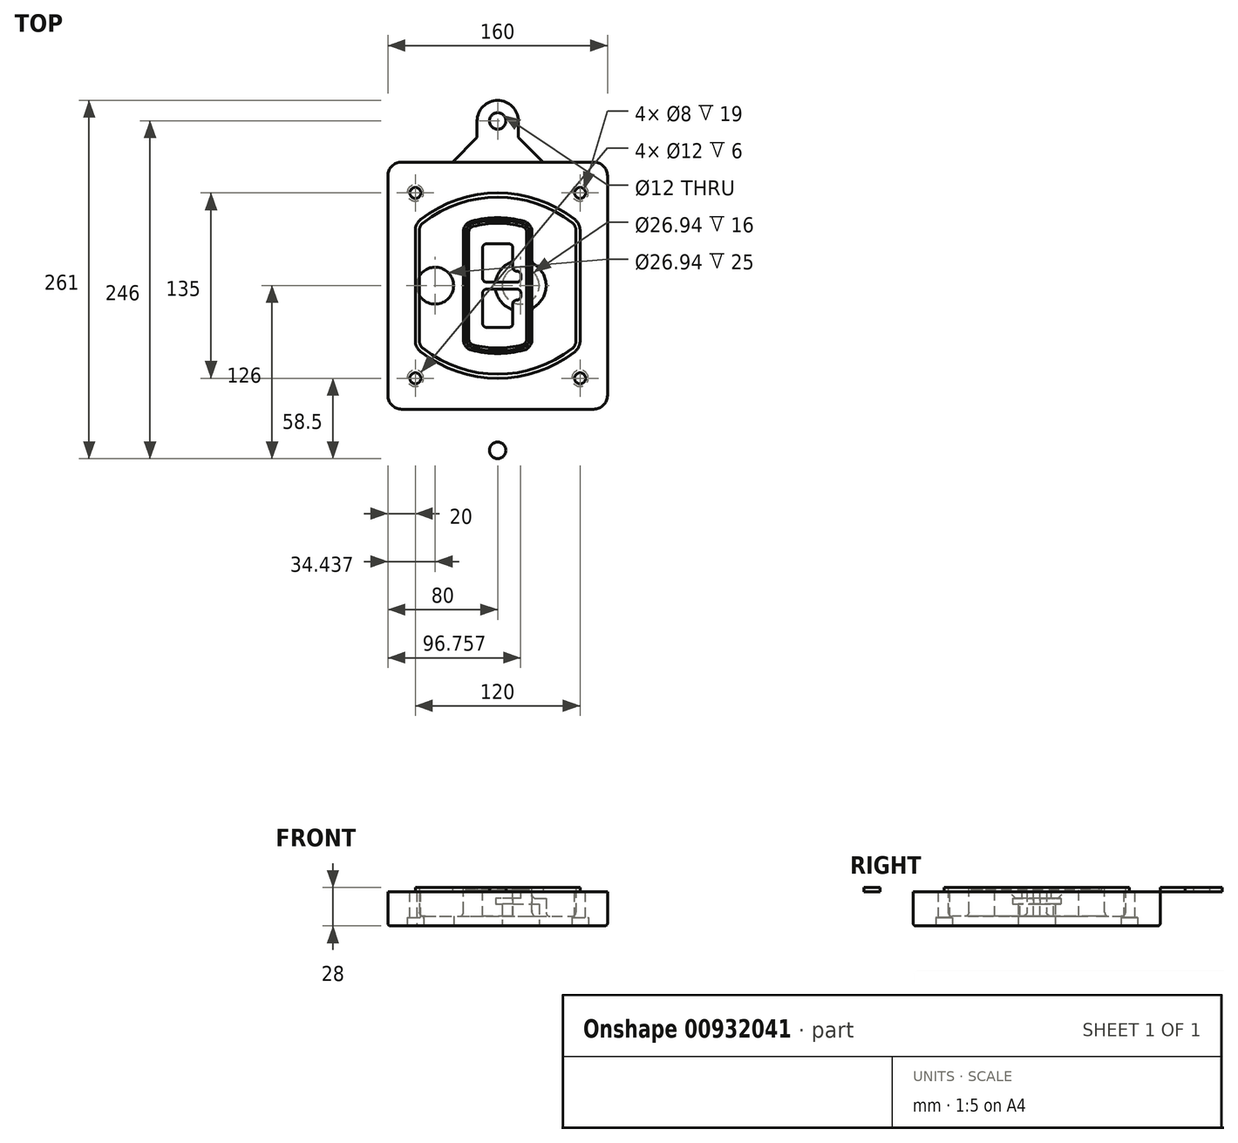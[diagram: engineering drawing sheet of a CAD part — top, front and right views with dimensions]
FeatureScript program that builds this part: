
annotation { "Feature Type Name" : "Feature", "Feature Type Description" : "" }
export const myFeature = defineFeature(function(context is Context, id is Id, definition is map)
    precondition{}
    {
        {
            var Q0;
            Q0=qCreatedBy(makeId("Top.planeOp"),FACE);
            var sketch = newSketch(context, id + "F0", { "sketchPlane" : qUnion([Q0])});
            skPoint(sketch, "E0.rect.middle", {"position": v(0, 0) * mm});
            skLineSegment(sketch, "E1.bottom", {"start": v(-70, -90) * mm, "end": v(70, -90) * mm});
            skLineSegment(sketch, "E1.top", {"start": v(-70, 90) * mm, "end": v(70, 90) * mm});
            skLineSegment(sketch, "E1.left", {"start": v(-80, -80) * mm, "end": v(-80, 80) * mm});
            skLineSegment(sketch, "E1.right", {"start": v(80, -80) * mm, "end": v(80, 80) * mm});
            skLineSegment(sketch, "E2", {"start": v(-80, 90) * mm, "end": v(80, -90) * mm, "construction": true});
            skLineSegment(sketch, "E3", {"start": v(80, 90) * mm, "end": v(-80, -90) * mm, "construction": true});
            skCircle(sketch, "E4", {"center": v(-60, 67.5) * mm, "radius": 4 * mm});
            skCircle(sketch, "E5", {"center": v(60, 67.5) * mm, "radius": 4 * mm});
            skCircle(sketch, "E6", {"center": v(60, -67.5) * mm, "radius": 4 * mm});
            skCircle(sketch, "E7", {"center": v(-60, -67.5) * mm, "radius": 4 * mm});
            skLineSegment(sketch, "E8", {"start": v(-60, 67.5) * mm, "end": v(60, 67.5) * mm, "construction": true});
            skLineSegment(sketch, "E9", {"start": v(60, 67.5) * mm, "end": v(60, -67.5) * mm, "construction": true});
            skLineSegment(sketch, "E10", {"start": v(60, -67.5) * mm, "end": v(-60, -67.5) * mm, "construction": true});
            skLineSegment(sketch, "E11", {"start": v(-60, -67.5) * mm, "end": v(-60, 67.5) * mm, "construction": true});
            skLineSegment(sketch, "E12", {"start": v(-60, 40.3) * mm, "end": v(-60, -40.3) * mm});
            skLineSegment(sketch, "E13", {"start": v(60, 40.3) * mm, "end": v(60, -40.3) * mm});
            skArc(sketch, "E14", {"start": v(56.15, 48.18) * mm, "mid": v(0, 67.5) * mm, "end": v(-56.15, 48.18) * mm});
            skArc(sketch, "E15", {"start": v(-56.15, -48.18) * mm, "mid": v(0, -67.5) * mm, "end": v(56.15, -48.18) * mm});
            skLineSegment(sketch, "E16", {"start": v(-60, 0) * mm, "end": v(60, 0) * mm, "construction": true});
            skPoint(sketch, "E17.visualSharp", {"position": v(-60, -45) * mm});
            skArc(sketch, "E17.filletArc", {"start": v(-60, -40.3) * mm, "mid": v(-58.99, -44.68) * mm, "end": v(-56.15, -48.18) * mm});
            skPoint(sketch, "E18.visualSharp", {"position": v(-60, 45) * mm});
            skArc(sketch, "E18.filletArc", {"start": v(-56.15, 48.18) * mm, "mid": v(-58.99, 44.68) * mm, "end": v(-60, 40.3) * mm});
            skPoint(sketch, "E19.visualSharp", {"position": v(60, 45) * mm});
            skArc(sketch, "E19.filletArc", {"start": v(60, 40.3) * mm, "mid": v(58.99, 44.68) * mm, "end": v(56.15, 48.18) * mm});
            skPoint(sketch, "E20.visualSharp", {"position": v(60, -45) * mm});
            skArc(sketch, "E20.filletArc", {"start": v(56.15, -48.18) * mm, "mid": v(58.99, -44.68) * mm, "end": v(60, -40.3) * mm});
            skPoint(sketch, "E21.visualSharp", {"position": v(-80, 90) * mm});
            skArc(sketch, "E21.filletArc", {"start": v(-70, 90) * mm, "mid": v(-77.07, 87.07) * mm, "end": v(-80, 80) * mm});
            skPoint(sketch, "E22.visualSharp", {"position": v(80, 90) * mm});
            skArc(sketch, "E22.filletArc", {"start": v(80, 80) * mm, "mid": v(77.07, 87.07) * mm, "end": v(70, 90) * mm});
            skPoint(sketch, "E23.visualSharp", {"position": v(80, -90) * mm});
            skArc(sketch, "E23.filletArc", {"start": v(70, -90) * mm, "mid": v(77.07, -87.07) * mm, "end": v(80, -80) * mm});
            skPoint(sketch, "E24.visualSharp", {"position": v(-80, -90) * mm});
            skArc(sketch, "E24.filletArc", {"start": v(-80, -80) * mm, "mid": v(-77.07, -87.07) * mm, "end": v(-70, -90) * mm});
            skArc(sketch, "E25.0", {"start": v(57, 40.3) * mm, "mid": v(56.3, 43.36) * mm, "end": v(54.3, 45.81) * mm});
            skLineSegment(sketch, "E25.1", {"start": v(57, 40.3) * mm, "end": v(57, -40.3) * mm});
            skArc(sketch, "E25.2", {"start": v(54.3, -45.81) * mm, "mid": v(56.3, -43.36) * mm, "end": v(57, -40.3) * mm});
            skArc(sketch, "E25.3", {"start": v(-54.3, -45.81) * mm, "mid": v(0, -64.5) * mm, "end": v(54.3, -45.81) * mm});
            skArc(sketch, "E25.4", {"start": v(-57, -40.3) * mm, "mid": v(-56.3, -43.36) * mm, "end": v(-54.3, -45.81) * mm});
            skArc(sketch, "E25.5", {"start": v(54.3, 45.81) * mm, "mid": v(0, 64.5) * mm, "end": v(-54.3, 45.81) * mm});
            skLineSegment(sketch, "E25.6", {"start": v(-57, 40.3) * mm, "end": v(-57, -40.3) * mm});
            skArc(sketch, "E25.7", {"start": v(-54.3, 45.81) * mm, "mid": v(-56.3, 43.36) * mm, "end": v(-57, 40.3) * mm});
            skArc(sketch, "E26.0", {"start": v(-58.62, 51.33) * mm, "mid": v(-62.58, 46.43) * mm, "end": v(-64, 40.3) * mm});
            skArc(sketch, "E26.1", {"start": v(58.62, 51.33) * mm, "mid": v(0, 71.5) * mm, "end": v(-58.62, 51.33) * mm});
            skArc(sketch, "E26.2", {"start": v(64, 40.3) * mm, "mid": v(62.58, 46.43) * mm, "end": v(58.62, 51.33) * mm});
            skLineSegment(sketch, "E26.3", {"start": v(64, 40.3) * mm, "end": v(64, -40.3) * mm});
            skArc(sketch, "E26.4", {"start": v(58.62, -51.33) * mm, "mid": v(62.58, -46.43) * mm, "end": v(64, -40.3) * mm});
            skLineSegment(sketch, "E26.5", {"start": v(-64, 40.3) * mm, "end": v(-64, -40.3) * mm});
            skArc(sketch, "E26.6", {"start": v(-58.62, -51.33) * mm, "mid": v(0, -71.5) * mm, "end": v(58.62, -51.33) * mm});
            skArc(sketch, "E26.7", {"start": v(-64, -40.3) * mm, "mid": v(-62.58, -46.43) * mm, "end": v(-58.62, -51.33) * mm});
            skSolve(sketch);
        }
        {
            var Q0;
            Q0=makeQuery(id+"F0.imprint","IMPRINT",FACE,{"disambiguationData":[TD([[makeQuery(id+"F0.imprint","IMPRINT",EDGE,{"derivedFrom":sQuery(id+"F0.wireOp",EDGE,"E1.bottom")}),1.0]])]});
            var Q1;
            Q1=makeQuery(id+"F0.imprint","IMPRINT",FACE,{"disambiguationData":[TD([[makeQuery(id+"F0.imprint","IMPRINT",EDGE,{"derivedFrom":sQuery(id+"F0.wireOp",EDGE,"E12")}),1.0]])]});
            var Q2;
            Q2=makeQuery(id+"F0.imprint","IMPRINT",FACE,{"disambiguationData":[TD([[makeQuery(id+"F0.imprint","IMPRINT",EDGE,{"derivedFrom":sQuery(id+"F0.wireOp",EDGE,"E25.0")}),1.0]])]});
            var Q3;
            Q3=makeQuery(id+"F0.imprint","IMPRINT",FACE,{"disambiguationData":[TD([[makeQuery(id+"F0.imprint","IMPRINT",EDGE,{"derivedFrom":sQuery(id+"F0.wireOp",EDGE,"E12")}),-1.0]])]});
            extrude(context, id + "F1", {"entities" : qUnion([Q0, Q1, Q2, Q3]), "oppositeDirection" : true, "depth" : 25 * mm});
        }
        {
            var Q0;
            Q0=makeQuery(id+"F0.imprint","IMPRINT",FACE,{"disambiguationData":[TD([[makeQuery(id+"F0.imprint","IMPRINT",EDGE,{"derivedFrom":sQuery(id+"F0.wireOp",EDGE,"E12")}),1.0]])]});
            extrude(context, id + "F2", {"entities" : qUnion([Q0]), "operationType" : NewBodyOperationType.ADD, "depth" : 3 * mm});
        }
        {
            var Q0;
            Q0=makeQuery(id+"F0.imprint","IMPRINT",FACE,{"disambiguationData":[TD([[makeQuery(id+"F0.imprint","IMPRINT",EDGE,{"derivedFrom":sQuery(id+"F0.wireOp",EDGE,"E25.0")}),1.0]])]});
            extrude(context, id + "F3", {"entities" : qUnion([Q0]), "operationType" : NewBodyOperationType.REMOVE, "oppositeDirection" : true, "depth" : 18 * mm});
        }
        {
            var Q0;
            Q0=makeQuery(id+"F2.opExtrude","CAP_FACE",FACE,{"disambiguationData":[OSD([sQuery(id+"F0.wireOp",EDGE,"E12"),sQuery(id+"F0.wireOp",EDGE,"E13"),sQuery(id+"F0.wireOp",EDGE,"E14"),sQuery(id+"F0.wireOp",EDGE,"E15"),sQuery(id+"F0.wireOp",EDGE,"E17.filletArc"),sQuery(id+"F0.wireOp",EDGE,"E18.filletArc"),sQuery(id+"F0.wireOp",EDGE,"E19.filletArc"),sQuery(id+"F0.wireOp",EDGE,"E20.filletArc"),sQuery(id+"F0.wireOp",EDGE,"E25.0"),sQuery(id+"F0.wireOp",EDGE,"E25.1"),sQuery(id+"F0.wireOp",EDGE,"E25.2"),sQuery(id+"F0.wireOp",EDGE,"E25.3"),sQuery(id+"F0.wireOp",EDGE,"E25.4"),sQuery(id+"F0.wireOp",EDGE,"E25.5"),sQuery(id+"F0.wireOp",EDGE,"E25.6"),sQuery(id+"F0.wireOp",EDGE,"E25.7")])],"isStart":false});
            var sketch = newSketch(context, id + "F4", { "sketchPlane" : qUnion([Q0])});
            skArc(sketch, "E27.0", {"start": v(-19.08, -46.97) * mm, "mid": v(0, -49.5) * mm, "end": v(19.08, -46.97) * mm});
            skArc(sketch, "E28.0", {"start": v(19.08, 46.97) * mm, "mid": v(0, 49.5) * mm, "end": v(-19.08, 46.97) * mm});
            skLineSegment(sketch, "E29", {"start": v(-25, 39.25) * mm, "end": v(-25, -39.25) * mm});
            skLineSegment(sketch, "E30", {"start": v(25, 39.25) * mm, "end": v(25, -39.25) * mm});
            skLineSegment(sketch, "E31", {"start": v(-25, 45.1) * mm, "end": v(25, 45.1) * mm, "construction": true});
            skLineSegment(sketch, "E32", {"start": v(-25, -45.1) * mm, "end": v(25, -45.1) * mm, "construction": true});
            skPoint(sketch, "E33.visualSharp", {"position": v(-25, 45.1) * mm});
            skArc(sketch, "E33.filletArc", {"start": v(-19.08, 46.97) * mm, "mid": v(-23.35, 44.11) * mm, "end": v(-25, 39.25) * mm});
            skPoint(sketch, "E34.visualSharp", {"position": v(25, 45.1) * mm});
            skArc(sketch, "E34.filletArc", {"start": v(25, 39.25) * mm, "mid": v(23.35, 44.11) * mm, "end": v(19.08, 46.97) * mm});
            skPoint(sketch, "E35.visualSharp", {"position": v(25, -45.1) * mm});
            skArc(sketch, "E35.filletArc", {"start": v(19.08, -46.97) * mm, "mid": v(23.35, -44.11) * mm, "end": v(25, -39.25) * mm});
            skPoint(sketch, "E36.visualSharp", {"position": v(-25, -45.1) * mm});
            skArc(sketch, "E36.filletArc", {"start": v(-25, -39.25) * mm, "mid": v(-23.35, -44.11) * mm, "end": v(-19.08, -46.97) * mm});
            skArc(sketch, "E37.0", {"start": v(54.3, 45.81) * mm, "mid": v(0, 64.5) * mm, "end": v(-54.3, 45.81) * mm});
            skArc(sketch, "E37.1", {"start": v(-54.3, 45.81) * mm, "mid": v(-56.3, 43.36) * mm, "end": v(-57, 40.3) * mm});
            skLineSegment(sketch, "E37.2", {"start": v(-57, 40.3) * mm, "end": v(-57, -40.3) * mm});
            skArc(sketch, "E37.3", {"start": v(-57, -40.3) * mm, "mid": v(-56.3, -43.36) * mm, "end": v(-54.3, -45.81) * mm});
            skArc(sketch, "E37.4", {"start": v(-54.3, -45.81) * mm, "mid": v(0, -64.5) * mm, "end": v(54.3, -45.81) * mm});
            skArc(sketch, "E37.5", {"start": v(54.3, -45.81) * mm, "mid": v(56.3, -43.36) * mm, "end": v(57, -40.3) * mm});
            skLineSegment(sketch, "E37.6", {"start": v(57, 40.3) * mm, "end": v(57, -40.3) * mm});
            skArc(sketch, "E37.7", {"start": v(57, 40.3) * mm, "mid": v(56.3, 43.36) * mm, "end": v(54.3, 45.81) * mm});
            skLineSegment(sketch, "E38.0", {"start": v(23, 39.25) * mm, "end": v(23, -39.25) * mm});
            skArc(sketch, "E38.1", {"start": v(18.56, -45.04) * mm, "mid": v(21.76, -42.9) * mm, "end": v(23, -39.25) * mm});
            skArc(sketch, "E38.2", {"start": v(-18.56, -45.04) * mm, "mid": v(0, -47.5) * mm, "end": v(18.56, -45.04) * mm});
            skArc(sketch, "E38.3", {"start": v(-23, -39.25) * mm, "mid": v(-21.76, -42.9) * mm, "end": v(-18.56, -45.04) * mm});
            skLineSegment(sketch, "E38.4", {"start": v(-23, 39.25) * mm, "end": v(-23, -39.25) * mm});
            skArc(sketch, "E38.5", {"start": v(23, 39.25) * mm, "mid": v(21.76, 42.9) * mm, "end": v(18.56, 45.04) * mm});
            skArc(sketch, "E38.6", {"start": v(-18.56, 45.04) * mm, "mid": v(-21.76, 42.9) * mm, "end": v(-23, 39.25) * mm});
            skArc(sketch, "E38.7", {"start": v(18.56, 45.04) * mm, "mid": v(0, 47.5) * mm, "end": v(-18.56, 45.04) * mm});
            skArc(sketch, "E39.0", {"start": v(21, 39.25) * mm, "mid": v(20.18, 41.68) * mm, "end": v(18.04, 43.1) * mm});
            skLineSegment(sketch, "E39.1", {"start": v(21, 39.25) * mm, "end": v(21, -39.25) * mm});
            skArc(sketch, "E39.2", {"start": v(18.04, -43.1) * mm, "mid": v(20.18, -41.68) * mm, "end": v(21, -39.25) * mm});
            skArc(sketch, "E39.3", {"start": v(-18.04, -43.1) * mm, "mid": v(0, -45.5) * mm, "end": v(18.04, -43.1) * mm});
            skArc(sketch, "E39.4", {"start": v(-21, -39.25) * mm, "mid": v(-20.18, -41.68) * mm, "end": v(-18.04, -43.1) * mm});
            skArc(sketch, "E39.5", {"start": v(18.04, 43.1) * mm, "mid": v(0, 45.5) * mm, "end": v(-18.04, 43.1) * mm});
            skLineSegment(sketch, "E39.6", {"start": v(-21, 39.25) * mm, "end": v(-21, -39.25) * mm});
            skArc(sketch, "E39.7", {"start": v(-18.04, 43.1) * mm, "mid": v(-20.18, 41.68) * mm, "end": v(-21, 39.25) * mm});
            skLineSegment(sketch, "E40", {"start": v(-25, 0) * mm, "end": v(25, 0) * mm, "construction": true});
            skLineSegment(sketch, "E41", {"start": v(-11, 5.5) * mm, "end": v(-11, 27.5) * mm});
            skLineSegment(sketch, "E42", {"start": v(-8, 30.5) * mm, "end": v(8, 30.5) * mm});
            skLineSegment(sketch, "E43", {"start": v(11, 27.5) * mm, "end": v(11, 13.5) * mm});
            skLineSegment(sketch, "E44", {"start": v(14, 10.5) * mm, "end": v(14, 10.5) * mm});
            skLineSegment(sketch, "E45", {"start": v(17, 7.5) * mm, "end": v(17, 5.5) * mm});
            skLineSegment(sketch, "E46", {"start": v(14, 2.5) * mm, "end": v(-8, 2.5) * mm});
            skPoint(sketch, "E47.visualSharp", {"position": v(-11, 30.5) * mm});
            skArc(sketch, "E47.filletArc", {"start": v(-8, 30.5) * mm, "mid": v(-10.12, 29.62) * mm, "end": v(-11, 27.5) * mm});
            skPoint(sketch, "E48.visualSharp", {"position": v(11, 30.5) * mm});
            skArc(sketch, "E48.filletArc", {"start": v(11, 27.5) * mm, "mid": v(10.12, 29.62) * mm, "end": v(8, 30.5) * mm});
            skPoint(sketch, "E49.visualSharp", {"position": v(11, 10.5) * mm});
            skArc(sketch, "E49.filletArc", {"start": v(11, 13.5) * mm, "mid": v(11.88, 11.38) * mm, "end": v(14, 10.5) * mm});
            skPoint(sketch, "E50.visualSharp", {"position": v(17, 10.5) * mm});
            skArc(sketch, "E50.filletArc", {"start": v(17, 7.5) * mm, "mid": v(16.12, 9.62) * mm, "end": v(14, 10.5) * mm});
            skPoint(sketch, "E51.visualSharp", {"position": v(17, 2.5) * mm});
            skArc(sketch, "E51.filletArc", {"start": v(14, 2.5) * mm, "mid": v(16.12, 3.38) * mm, "end": v(17, 5.5) * mm});
            skPoint(sketch, "E52.visualSharp", {"position": v(-11, 2.5) * mm});
            skArc(sketch, "E52.filletArc", {"start": v(-11, 5.5) * mm, "mid": v(-10.12, 3.38) * mm, "end": v(-8, 2.5) * mm});
            skLineSegment(sketch, "E53.0.MirrorCS", {"start": v(14, -2.5) * mm, "end": v(-8, -2.5) * mm});
            skArc(sketch, "E54.0.MirrorCS", {"start": v(-11, -5.5) * mm, "mid": v(-10.12, -3.38) * mm, "end": v(-8, -2.5) * mm});
            skLineSegment(sketch, "E55.0.MirrorCS", {"start": v(-11, -5.5) * mm, "end": v(-11, -27.5) * mm});
            skArc(sketch, "E56.0.MirrorCS", {"start": v(-8, -30.5) * mm, "mid": v(-10.12, -29.62) * mm, "end": v(-11, -27.5) * mm});
            skLineSegment(sketch, "E57.0.MirrorCS", {"start": v(-8, -30.5) * mm, "end": v(8, -30.5) * mm});
            skArc(sketch, "E58.0.MirrorCS", {"start": v(11, -27.5) * mm, "mid": v(10.12, -29.62) * mm, "end": v(8, -30.5) * mm});
            skLineSegment(sketch, "E59.0.MirrorCS", {"start": v(11, -27.5) * mm, "end": v(11, -13.5) * mm});
            skArc(sketch, "E60.0.MirrorCS", {"start": v(11, -13.5) * mm, "mid": v(11.88, -11.38) * mm, "end": v(14, -10.5) * mm});
            skArc(sketch, "E61.0.MirrorCS", {"start": v(17, -7.5) * mm, "mid": v(16.12, -9.62) * mm, "end": v(14, -10.5) * mm});
            skLineSegment(sketch, "E62.0.MirrorCS", {"start": v(17, -7.5) * mm, "end": v(17, -5.5) * mm});
            skArc(sketch, "E63.0.MirrorCS", {"start": v(14, -2.5) * mm, "mid": v(16.12, -3.38) * mm, "end": v(17, -5.5) * mm});
            skSolve(sketch);
        }
        {
            var Q0;
            Q0=makeQuery(id+"F4.imprint","IMPRINT",FACE,{"disambiguationData":[TD([[makeQuery(id+"F4.imprint","IMPRINT",EDGE,{"derivedFrom":sQuery(id+"F4.wireOp",EDGE,"E27.0")}),1.0]])]});
            var Q1;
            Q1=makeQuery(id+"F4.imprint","IMPRINT",FACE,{"disambiguationData":[TD([[makeQuery(id+"F4.imprint","IMPRINT",EDGE,{"derivedFrom":sQuery(id+"F4.wireOp",EDGE,"E38.0")}),-1.0]])]});
            var Q2;
            Q2=makeQuery(id+"F4.imprint","IMPRINT",FACE,{"disambiguationData":[TD([[makeQuery(id+"F4.imprint","IMPRINT",EDGE,{"derivedFrom":sQuery(id+"F4.wireOp",EDGE,"E39.0")}),1.0]])]});
            extrude(context, id + "F5", {"entities" : qUnion([Q0, Q1, Q2]), "operationType" : NewBodyOperationType.ADD, "endBound" : BoundingType.UP_TO_NEXT, "oppositeDirection" : true, "depth" : 25 * mm});
        }
        {
            var Q0;
            Q0=makeQuery(id+"F4.imprint","IMPRINT",FACE,{"disambiguationData":[TD([[makeQuery(id+"F4.imprint","IMPRINT",EDGE,{"derivedFrom":sQuery(id+"F4.wireOp",EDGE,"E38.0")}),-1.0]])]});
            extrude(context, id + "F6", {"entities" : qUnion([Q0]), "operationType" : NewBodyOperationType.REMOVE, "oppositeDirection" : true, "depth" : 2 * mm});
        }
        {
            var Q0;
            Q0=makeQuery(id+"F1.opExtrude","CAP_FACE",FACE,{"disambiguationData":[OSD([sQuery(id+"F0.wireOp",EDGE,"E1.bottom"),sQuery(id+"F0.wireOp",EDGE,"E1.top"),sQuery(id+"F0.wireOp",EDGE,"E1.left"),sQuery(id+"F0.wireOp",EDGE,"E1.right"),sQuery(id+"F0.wireOp",EDGE,"E4"),sQuery(id+"F0.wireOp",EDGE,"E5"),sQuery(id+"F0.wireOp",EDGE,"E6"),sQuery(id+"F0.wireOp",EDGE,"E7"),sQuery(id+"F0.wireOp",EDGE,"E21.filletArc"),sQuery(id+"F0.wireOp",EDGE,"E22.filletArc"),sQuery(id+"F0.wireOp",EDGE,"E23.filletArc"),sQuery(id+"F0.wireOp",EDGE,"E24.filletArc")])],"isStart":false});
            var sketch = newSketch(context, id + "F7", { "sketchPlane" : qUnion([Q0])});
            skCircle(sketch, "E64", {"center": v(16.76, 0) * mm, "radius": 13.47 * mm});
            skCircle(sketch, "E65", {"center": v(-45.56, 0) * mm, "radius": 13.47 * mm});
            skLineSegment(sketch, "E66", {"start": v(80, 0) * mm, "end": v(-80, 0) * mm});
            skCircle(sketch, "E67", {"center": v(16.76, 0) * mm, "radius": 18.47 * mm});
            skCircle(sketch, "E68", {"center": v(60, -67.5) * mm, "radius": 6 * mm});
            skCircle(sketch, "E69", {"center": v(-60, -67.5) * mm, "radius": 6 * mm});
            skCircle(sketch, "E70", {"center": v(-60, 67.5) * mm, "radius": 6 * mm});
            skCircle(sketch, "E71", {"center": v(60, 67.5) * mm, "radius": 6 * mm});
            skSolve(sketch);
        }
        {
            var Q0;
            {var subQ1=sQuery(id+"F7.wireOp",EDGE,"E66");var subQ4=sQuery(id+"F7.wireOp",EDGE,"E64");var subQ6=makeQuery(id+"F7.imprint","INTERSECT",VERTEX,{"disambiguationData":[OD(0.0)],"derivedFrom":[subQ4,subQ1]});Q0=makeQuery(id+"F7.imprint","IMPRINT",FACE,{"disambiguationData":[TD([[makeQuery(id+"F7.imprint","IMPRINT",EDGE,{"disambiguationData":[TD([[subQ6,-1.0]])],"derivedFrom":subQ4}),-1.0]])]});}
            var Q1;
            {var subQ0=sQuery(id+"F7.wireOp",EDGE,"E66");var subQ1=sQuery(id+"F7.wireOp",EDGE,"E64");var subQ3=makeQuery(id+"F7.imprint","INTERSECT",VERTEX,{"disambiguationData":[OD(0.0)],"derivedFrom":[subQ1,subQ0]});Q1=makeQuery(id+"F7.imprint","IMPRINT",FACE,{"disambiguationData":[TD([[makeQuery(id+"F7.imprint","IMPRINT",EDGE,{"disambiguationData":[TD([[subQ3,-1.0]])],"derivedFrom":subQ1}),1.0]])]});}
            var Q2;
            {var subQ0=sQuery(id+"F7.wireOp",EDGE,"E66");var subQ1=sQuery(id+"F7.wireOp",EDGE,"E64");var subQ3=makeQuery(id+"F7.imprint","INTERSECT",VERTEX,{"disambiguationData":[OD(0.0)],"derivedFrom":[subQ1,subQ0]});Q2=makeQuery(id+"F7.imprint","IMPRINT",FACE,{"disambiguationData":[TD([[makeQuery(id+"F7.imprint","IMPRINT",EDGE,{"disambiguationData":[TD([[subQ3,1.0]])],"derivedFrom":subQ1}),1.0]])]});}
            var Q3;
            {var subQ1=sQuery(id+"F7.wireOp",EDGE,"E66");var subQ4=sQuery(id+"F7.wireOp",EDGE,"E64");var subQ6=makeQuery(id+"F7.imprint","INTERSECT",VERTEX,{"disambiguationData":[OD(0.0)],"derivedFrom":[subQ4,subQ1]});Q3=makeQuery(id+"F7.imprint","IMPRINT",FACE,{"disambiguationData":[TD([[makeQuery(id+"F7.imprint","IMPRINT",EDGE,{"disambiguationData":[TD([[subQ6,1.0]])],"derivedFrom":subQ4}),-1.0]])]});}
            extrude(context, id + "F8", {"entities" : qUnion([Q0, Q1, Q2, Q3]), "operationType" : NewBodyOperationType.ADD, "oppositeDirection" : true, "depth" : 20 * mm});
        }
        {
            var Q0;
            {var subQ0=sQuery(id+"F7.wireOp",EDGE,"E66");var subQ1=sQuery(id+"F7.wireOp",EDGE,"E64");var subQ3=makeQuery(id+"F7.imprint","INTERSECT",VERTEX,{"disambiguationData":[OD(0.0)],"derivedFrom":[subQ1,subQ0]});Q0=makeQuery(id+"F7.imprint","IMPRINT",FACE,{"disambiguationData":[TD([[makeQuery(id+"F7.imprint","IMPRINT",EDGE,{"disambiguationData":[TD([[subQ3,-1.0]])],"derivedFrom":subQ1}),1.0]])]});}
            var Q1;
            {var subQ0=sQuery(id+"F7.wireOp",EDGE,"E66");var subQ1=sQuery(id+"F7.wireOp",EDGE,"E64");var subQ3=makeQuery(id+"F7.imprint","INTERSECT",VERTEX,{"disambiguationData":[OD(0.0)],"derivedFrom":[subQ1,subQ0]});Q1=makeQuery(id+"F7.imprint","IMPRINT",FACE,{"disambiguationData":[TD([[makeQuery(id+"F7.imprint","IMPRINT",EDGE,{"disambiguationData":[TD([[subQ3,1.0]])],"derivedFrom":subQ1}),1.0]])]});}
            extrude(context, id + "F9", {"entities" : qUnion([Q0, Q1]), "operationType" : NewBodyOperationType.REMOVE, "oppositeDirection" : true, "depth" : 16 * mm});
        }
        {
            var Q0;
            {var subQ0=sQuery(id+"F7.wireOp",EDGE,"E66");var subQ1=sQuery(id+"F7.wireOp",EDGE,"E65");var subQ3=makeQuery(id+"F7.imprint","INTERSECT",VERTEX,{"disambiguationData":[OD(0.0)],"derivedFrom":[subQ1,subQ0]});Q0=makeQuery(id+"F7.imprint","IMPRINT",FACE,{"disambiguationData":[TD([[makeQuery(id+"F7.imprint","IMPRINT",EDGE,{"disambiguationData":[TD([[subQ3,-1.0]])],"derivedFrom":subQ1}),1.0]])]});}
            var Q1;
            {var subQ0=sQuery(id+"F7.wireOp",EDGE,"E66");var subQ1=sQuery(id+"F7.wireOp",EDGE,"E65");var subQ3=makeQuery(id+"F7.imprint","INTERSECT",VERTEX,{"disambiguationData":[OD(0.0)],"derivedFrom":[subQ1,subQ0]});Q1=makeQuery(id+"F7.imprint","IMPRINT",FACE,{"disambiguationData":[TD([[makeQuery(id+"F7.imprint","IMPRINT",EDGE,{"disambiguationData":[TD([[subQ3,1.0]])],"derivedFrom":subQ1}),1.0]])]});}
            extrude(context, id + "F10", {"entities" : qUnion([Q0, Q1]), "operationType" : NewBodyOperationType.REMOVE, "oppositeDirection" : true, "depth" : 25 * mm});
        }
        {
            var Q0;
            Q0=makeQuery(id+"F7.imprint","IMPRINT",FACE,{"disambiguationData":[TD([[makeQuery(id+"F7.imprint","IMPRINT",EDGE,{"derivedFrom":sQuery(id+"F7.wireOp",EDGE,"E68")}),1.0]])]});
            var Q1;
            Q1=makeQuery(id+"F7.imprint","IMPRINT",FACE,{"disambiguationData":[TD([[makeQuery(id+"F7.imprint","IMPRINT",EDGE,{"derivedFrom":makeQuery(id+"F1.opExtrude","CAP_EDGE",EDGE,{"disambiguationData":[OSD([sQuery(id+"F0.wireOp",EDGE,"E5")])],"isStart":false})}),-1.0]])]});
            var Q2;
            Q2=makeQuery(id+"F7.imprint","IMPRINT",FACE,{"disambiguationData":[TD([[makeQuery(id+"F7.imprint","IMPRINT",EDGE,{"derivedFrom":sQuery(id+"F7.wireOp",EDGE,"E69")}),1.0]])]});
            var Q3;
            Q3=makeQuery(id+"F7.imprint","IMPRINT",FACE,{"disambiguationData":[TD([[makeQuery(id+"F7.imprint","IMPRINT",EDGE,{"derivedFrom":makeQuery(id+"F1.opExtrude","CAP_EDGE",EDGE,{"disambiguationData":[OSD([sQuery(id+"F0.wireOp",EDGE,"E4")])],"isStart":false})}),-1.0]])]});
            var Q4;
            Q4=makeQuery(id+"F7.imprint","IMPRINT",FACE,{"disambiguationData":[TD([[makeQuery(id+"F7.imprint","IMPRINT",EDGE,{"derivedFrom":sQuery(id+"F7.wireOp",EDGE,"E70")}),1.0]])]});
            var Q5;
            Q5=makeQuery(id+"F7.imprint","IMPRINT",FACE,{"disambiguationData":[TD([[makeQuery(id+"F7.imprint","IMPRINT",EDGE,{"derivedFrom":makeQuery(id+"F1.opExtrude","CAP_EDGE",EDGE,{"disambiguationData":[OSD([sQuery(id+"F0.wireOp",EDGE,"E7")])],"isStart":false})}),-1.0]])]});
            var Q6;
            Q6=makeQuery(id+"F7.imprint","IMPRINT",FACE,{"disambiguationData":[TD([[makeQuery(id+"F7.imprint","IMPRINT",EDGE,{"derivedFrom":sQuery(id+"F7.wireOp",EDGE,"E71")}),1.0]])]});
            var Q7;
            Q7=makeQuery(id+"F7.imprint","IMPRINT",FACE,{"disambiguationData":[TD([[makeQuery(id+"F7.imprint","IMPRINT",EDGE,{"derivedFrom":makeQuery(id+"F1.opExtrude","CAP_EDGE",EDGE,{"disambiguationData":[OSD([sQuery(id+"F0.wireOp",EDGE,"E6")])],"isStart":false})}),-1.0]])]});
            extrude(context, id + "F11", {"entities" : qUnion([Q0, Q1, Q2, Q3, Q4, Q5, Q6, Q7]), "operationType" : NewBodyOperationType.REMOVE, "oppositeDirection" : true, "depth" : 6 * mm});
        }
        {
            var Q0;
            Q0=makeQuery(id+"F9.boolean.opBoolean","COPY",FACE,{"derivedFrom":makeQuery(id+"F9.opExtrude","CAP_FACE",FACE,{"disambiguationData":[OSD([sQuery(id+"F7.wireOp",EDGE,"E64")])],"isStart":false})});
            var sketch = newSketch(context, id + "F12", { "sketchPlane" : qUnion([Q0])});
            skArc(sketch, "E72.0", {"start": v(11, 17.55) * mm, "mid": v(2.57, 11.82) * mm, "end": v(-1.54, 2.5) * mm});
            skArc(sketch, "E72.1", {"start": v(-1.54, -2.5) * mm, "mid": v(2.57, -11.82) * mm, "end": v(11, -17.55) * mm});
            skLineSegment(sketch, "E73", {"start": v(-1.54, -2.5) * mm, "end": v(14, -2.5) * mm});
            skLineSegment(sketch, "E74.0", {"start": v(14, 2.5) * mm, "end": v(-1.54, 2.5) * mm});
            skArc(sketch, "E74.1", {"start": v(14, 2.5) * mm, "mid": v(16.12, 3.38) * mm, "end": v(17, 5.5) * mm});
            skLineSegment(sketch, "E74.2", {"start": v(17, 7.5) * mm, "end": v(17, 5.5) * mm});
            skArc(sketch, "E74.3", {"start": v(17, 7.5) * mm, "mid": v(16.12, 9.62) * mm, "end": v(14, 10.5) * mm});
            skArc(sketch, "E74.4", {"start": v(11, 13.5) * mm, "mid": v(11.88, 11.38) * mm, "end": v(14, 10.5) * mm});
            skLineSegment(sketch, "E74.5", {"start": v(11, 17.55) * mm, "end": v(11, 13.5) * mm});
            skLineSegment(sketch, "E74.7", {"start": v(14, -2.5) * mm, "end": v(-1.54, -2.5) * mm});
            skArc(sketch, "E74.8", {"start": v(14, -2.5) * mm, "mid": v(16.12, -3.38) * mm, "end": v(17, -5.5) * mm});
            skLineSegment(sketch, "E74.9", {"start": v(17, -7.5) * mm, "end": v(17, -5.5) * mm});
            skArc(sketch, "E74.10", {"start": v(17, -7.5) * mm, "mid": v(16.12, -9.62) * mm, "end": v(14, -10.5) * mm});
            skArc(sketch, "E74.11", {"start": v(11, -13.5) * mm, "mid": v(11.88, -11.38) * mm, "end": v(14, -10.5) * mm});
            skLineSegment(sketch, "E74.12", {"start": v(11, -17.55) * mm, "end": v(11, -13.5) * mm});
            skPoint(sketch, "E75.orphan", {"position": v(11, -27.5) * mm});
            skPoint(sketch, "E76.orphan", {"position": v(-8, -2.5) * mm});
            skPoint(sketch, "E77.orphan", {"position": v(-8, 2.5) * mm});
            skPoint(sketch, "E78.orphan", {"position": v(11, 27.5) * mm});
            skSolve(sketch);
        }
        {
            var Q0;
            {var subQ7=sQuery(id+"F12.wireOp",EDGE,"E72.0");var subQ14=sQuery(id+"F12.wireOp",EDGE,"E72.1");var subQ16=sQuery(id+"F12.wireOp",EDGE,"E74.1");var subQ18=sQuery(id+"F12.wireOp",EDGE,"E74.8");Q0=qUnion([makeQuery(id+"F12.imprint","IMPRINT",FACE,{"disambiguationData":[TD([[makeQuery(id+"F12.imprint","IMPRINT",EDGE,{"derivedFrom":subQ7}),1.0]])]}),makeQuery(id+"F12.imprint","IMPRINT",FACE,{"disambiguationData":[TD([[makeQuery(id+"F12.imprint","IMPRINT",EDGE,{"derivedFrom":subQ14}),1.0]])]}),makeQuery(id+"F12.imprint","IMPRINT",FACE,{"disambiguationData":[TD([[makeQuery(id+"F12.imprint","IMPRINT",EDGE,{"derivedFrom":subQ16}),1.0]])]}),makeQuery(id+"F12.imprint","IMPRINT",FACE,{"disambiguationData":[TD([[makeQuery(id+"F12.imprint","IMPRINT",EDGE,{"derivedFrom":subQ18}),-1.0]])]})]);}
            var Q1;
            Q1=makeQuery(id+"F5.boolean.opBoolean","SPLIT",FACE,{"disambiguationData":[TD([makeQuery(id+"F5.opExtrude","SWEPT_FACE",FACE,{"disambiguationData":[OSD([sQuery(id+"F4.wireOp",EDGE,"E41")])]})])],"derivedFrom":makeQuery(id+"F3.boolean.opBoolean","COPY",FACE,{"derivedFrom":makeQuery(id+"F3.opExtrude","CAP_FACE",FACE,{"disambiguationData":[OSD([sQuery(id+"F0.wireOp",EDGE,"E25.0"),sQuery(id+"F0.wireOp",EDGE,"E25.1"),sQuery(id+"F0.wireOp",EDGE,"E25.2"),sQuery(id+"F0.wireOp",EDGE,"E25.3"),sQuery(id+"F0.wireOp",EDGE,"E25.4"),sQuery(id+"F0.wireOp",EDGE,"E25.5"),sQuery(id+"F0.wireOp",EDGE,"E25.6"),sQuery(id+"F0.wireOp",EDGE,"E25.7")])],"isStart":false})})});
            extrude(context, id + "F13", {"entities" : qUnion([Q0]), "operationType" : NewBodyOperationType.REMOVE, "endBound" : BoundingType.UP_TO_SURFACE, "endBoundEntityFace" : qUnion([Q1]), "depth" : 25 * mm});
        }
        {
            var Q0;
            Q0=makeQuery(id+"F3.boolean.opBoolean","COPY",EDGE,{"derivedFrom":makeQuery(id+"F3.opExtrude","CAP_EDGE",EDGE,{"disambiguationData":[OSD([sQuery(id+"F0.wireOp",EDGE,"E25.6")])],"isStart":false})});
            var Q1;
            Q1=makeQuery(id+"F8.boolean.opBoolean","INTERSECT",EDGE,{"derivedFrom":[makeQuery(id+"F5.opExtrude","SWEPT_FACE",FACE,{"disambiguationData":[OSD([sQuery(id+"F4.wireOp",EDGE,"E30")])]}),makeQuery(id+"F8.opExtrude","CAP_FACE",FACE,{"disambiguationData":[OSD([sQuery(id+"F7.wireOp",EDGE,"E67")])],"isStart":false})]});
            var Q2;
            Q2=makeQuery(id+"F8.boolean.opBoolean","INTERSECT",EDGE,{"disambiguationData":[OD(1.0)],"derivedFrom":[makeQuery(id+"F5.opExtrude","SWEPT_FACE",FACE,{"disambiguationData":[OSD([sQuery(id+"F4.wireOp",EDGE,"E30")])]}),makeQuery(id+"F8.opExtrude","SWEPT_FACE",FACE,{"disambiguationData":[OSD([sQuery(id+"F7.wireOp",EDGE,"E67")])]})]});
            var Q3;
            {var subQ0=sQuery(id+"F4.wireOp",EDGE,"E30");Q3=makeQuery(id+"F8.boolean.opBoolean","SPLIT",EDGE,{"disambiguationData":[TD([makeQuery(id+"F5.opExtrude","SWEPT_FACE",FACE,{"disambiguationData":[OSD([sQuery(id+"F4.wireOp",EDGE,"E35.filletArc")])]})])],"derivedFrom":makeQuery(id+"F5.opExtrude","CAP_EDGE",EDGE,{"disambiguationData":[OSD([subQ0])],"isStart":false})});}
            var Q4;
            {var subQ0=sQuery(id+"F0.wireOp",EDGE,"E25.7");var subQ1=sQuery(id+"F0.wireOp",EDGE,"E25.1");var subQ2=sQuery(id+"F0.wireOp",EDGE,"E25.6");var subQ3=sQuery(id+"F0.wireOp",EDGE,"E25.5");var subQ4=sQuery(id+"F0.wireOp",EDGE,"E25.4");var subQ5=sQuery(id+"F0.wireOp",EDGE,"E25.0");var subQ6=sQuery(id+"F0.wireOp",EDGE,"E25.2");var subQ7=sQuery(id+"F0.wireOp",EDGE,"E25.3");Q4=makeQuery(id+"F8.boolean.opBoolean","INTERSECT",EDGE,{"derivedFrom":[makeQuery(id+"F5.boolean.opBoolean","SPLIT",FACE,{"disambiguationData":[TD([makeQuery(id+"F2.opExtrude","SWEPT_FACE",FACE,{"disambiguationData":[OSD([subQ5])]})])],"derivedFrom":makeQuery(id+"F3.boolean.opBoolean","COPY",FACE,{"derivedFrom":makeQuery(id+"F3.opExtrude","CAP_FACE",FACE,{"disambiguationData":[OSD([subQ5,subQ1,subQ6,subQ7,subQ4,subQ3,subQ2,subQ0])],"isStart":false})})}),makeQuery(id+"F8.opExtrude","SWEPT_FACE",FACE,{"disambiguationData":[OSD([sQuery(id+"F7.wireOp",EDGE,"E67")])]})]});}
            var Q5;
            Q5=makeQuery(id+"F8.boolean.opBoolean","INTERSECT",EDGE,{"disambiguationData":[OD(0.0)],"derivedFrom":[makeQuery(id+"F5.opExtrude","SWEPT_FACE",FACE,{"disambiguationData":[OSD([sQuery(id+"F4.wireOp",EDGE,"E30")])]}),makeQuery(id+"F8.opExtrude","SWEPT_FACE",FACE,{"disambiguationData":[OSD([sQuery(id+"F7.wireOp",EDGE,"E67")])]})]});
            fillet(context, id + "F14", {"entities" : qUnion([Q0, Q1, Q2, Q3, Q4, Q5]), "radius" : 3 * mm, "tangentPropagation" : true, "allowEdgeOverflow" : false});
        }
        {
            var Q0;
            Q0=makeQuery(id+"F1.opExtrude","CAP_EDGE",EDGE,{"disambiguationData":[OSD([sQuery(id+"F0.wireOp",EDGE,"E1.bottom")])],"isStart":false});
            fillet(context, id + "F15", {"entities" : qUnion([Q0]), "radius" : 2 * mm, "tangentPropagation" : true, "allowEdgeOverflow" : false});
        }
        {
            var Q0;
            {var subQ0=sQuery(id+"F0.wireOp",EDGE,"E21.filletArc");var subQ1=sQuery(id+"F0.wireOp",EDGE,"E7");var subQ2=sQuery(id+"F0.wireOp",EDGE,"E6");var subQ3=sQuery(id+"F0.wireOp",EDGE,"E5");var subQ4=sQuery(id+"F0.wireOp",EDGE,"E4");var subQ5=sQuery(id+"F0.wireOp",EDGE,"E22.filletArc");var subQ6=sQuery(id+"F0.wireOp",EDGE,"E1.bottom");var subQ7=sQuery(id+"F0.wireOp",EDGE,"E1.right");var subQ8=sQuery(id+"F0.wireOp",EDGE,"E1.top");var subQ9=sQuery(id+"F0.wireOp",EDGE,"E1.left");var subQ10=sQuery(id+"F0.wireOp",EDGE,"E23.filletArc");var subQ11=sQuery(id+"F0.wireOp",EDGE,"E24.filletArc");Q0=makeQuery(id+"F2.boolean.opBoolean","SPLIT",FACE,{"disambiguationData":[TD([makeQuery(id+"F1.opExtrude","SWEPT_FACE",FACE,{"disambiguationData":[OSD([subQ6])]})])],"derivedFrom":makeQuery(id+"F1.opExtrude","CAP_FACE",FACE,{"disambiguationData":[OSD([subQ6,subQ8,subQ9,subQ7,subQ4,subQ3,subQ2,subQ1,subQ0,subQ5,subQ10,subQ11])],"isStart":true})});}
            var sketch = newSketch(context, id + "F16", { "sketchPlane" : qUnion([Q0])});
            skLineSegment(sketch, "E79", {"start": v(-33, 90) * mm, "end": v(-15, 108) * mm});
            skLineSegment(sketch, "E80", {"start": v(33, 90) * mm, "end": v(15, 108) * mm});
            skLineSegment(sketch, "E81", {"start": v(-15, 108) * mm, "end": v(-15, 120) * mm});
            skLineSegment(sketch, "E82", {"start": v(15, 108) * mm, "end": v(15, 120) * mm});
            skArc(sketch, "E83", {"start": v(15, 120) * mm, "mid": v(0, 135) * mm, "end": v(-15, 120) * mm});
            skCircle(sketch, "E84", {"center": v(0, 120) * mm, "radius": 6 * mm});
            skLineSegment(sketch, "E85", {"start": v(0, 90) * mm, "end": v(0, 120) * mm, "construction": true});
            skPoint(sketch, "E86.endSnap0", {"position": v(80, 0) * mm});
            skPoint(sketch, "E87.endSnap0", {"position": v(-80, 0) * mm});
            skLineSegment(sketch, "E88", {"start": v(-80, 0) * mm, "end": v(80, 0) * mm, "construction": true});
            skLineSegment(sketch, "E89.MirrorCS", {"start": v(15, -108) * mm, "end": v(15, -120) * mm});
            skCircle(sketch, "E90.MirrorC", {"center": v(0, -120) * mm, "radius": 6 * mm});
            skLineSegment(sketch, "E91.MirrorCS", {"start": v(0, -90) * mm, "end": v(0, -120) * mm, "construction": true});
            skLineSegment(sketch, "E92.MirrorCS", {"start": v(33, -90) * mm, "end": v(15, -108) * mm});
            skLineSegment(sketch, "E93.MirrorCS", {"start": v(-15, -108) * mm, "end": v(-15, -120) * mm});
            skLineSegment(sketch, "E94.MirrorCS", {"start": v(-33, -90) * mm, "end": v(-15, -108) * mm});
            skArc(sketch, "E95.MirrorCS", {"start": v(15, -120) * mm, "mid": v(0, -135) * mm, "end": v(-15, -120) * mm});
            skLineSegment(sketch, "E96.0", {"start": v(-70, 90) * mm, "end": v(70, 90) * mm});
            skLineSegment(sketch, "E96.1", {"start": v(-80, -80) * mm, "end": v(-80, 80) * mm});
            skArc(sketch, "E96.2", {"start": v(-70, 90) * mm, "mid": v(-77.07, 87.07) * mm, "end": v(-80, 80) * mm});
            skArc(sketch, "E96.3", {"start": v(80, 80) * mm, "mid": v(77.07, 87.07) * mm, "end": v(70, 90) * mm});
            skLineSegment(sketch, "E96.4", {"start": v(80, -80) * mm, "end": v(80, 80) * mm});
            skSolve(sketch);
        }
        {
            var Q0;
            Q0 = qSketchRegion(id + "F16", true);
            var Q1;
            Q1=makeQuery(id+"F2.opExtrude","CAP_FACE",FACE,{"disambiguationData":[OSD([sQuery(id+"F0.wireOp",EDGE,"E12"),sQuery(id+"F0.wireOp",EDGE,"E13"),sQuery(id+"F0.wireOp",EDGE,"E14"),sQuery(id+"F0.wireOp",EDGE,"E15"),sQuery(id+"F0.wireOp",EDGE,"E17.filletArc"),sQuery(id+"F0.wireOp",EDGE,"E18.filletArc"),sQuery(id+"F0.wireOp",EDGE,"E19.filletArc"),sQuery(id+"F0.wireOp",EDGE,"E20.filletArc"),sQuery(id+"F0.wireOp",EDGE,"E25.0"),sQuery(id+"F0.wireOp",EDGE,"E25.1"),sQuery(id+"F0.wireOp",EDGE,"E25.2"),sQuery(id+"F0.wireOp",EDGE,"E25.3"),sQuery(id+"F0.wireOp",EDGE,"E25.4"),sQuery(id+"F0.wireOp",EDGE,"E25.5"),sQuery(id+"F0.wireOp",EDGE,"E25.6"),sQuery(id+"F0.wireOp",EDGE,"E25.7")])],"isStart":false});
            extrude(context, id + "F17", {"entities" : qUnion([Q0]), "endBound" : BoundingType.UP_TO_SURFACE, "depth" : 25 * mm, "endBoundEntityFace" : qUnion([Q1]), "offsetDistance" : 25 * mm});
        }
    });
